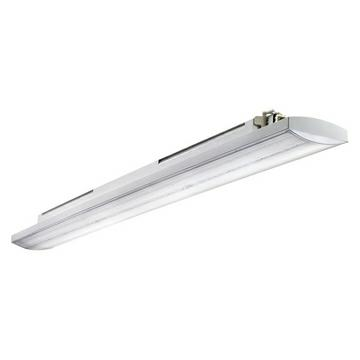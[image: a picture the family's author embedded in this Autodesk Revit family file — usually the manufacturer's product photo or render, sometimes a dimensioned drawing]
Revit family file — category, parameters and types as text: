
# Revit family: Lighting-Industrial-GEWISS-SMART[3]-WATERTIGHT-LED_TRASPARENT_1600mm
name_source: partatom
category: Apparecchi per illuminazione
units: mm (PartAtom-declared; Revit-internal decimal feet)

## family parameters
Condiviso = No
Host = Superficie
Punto di calcolo locali = Sì
Quota connettore circolare = Usa diametro
Sorgente d'illuminazione = No
Taglio con vuoti quando caricato = No
Tipo di parte = Normale

## types (1)
- Lighting-Industrial-GEWISS-SMART[3]-WATERTIGHT-LED_TRASPARENT_1600mm
    Application = Internal
    Catalogue = LIGHTING
    Catalogue Range = SMART [3]
    Colour temperature = 4000 K (CRI 80)
    Colour temperature: = 4000 K (CRI 80)
    Descrizione = SMART3 1600 72LED TRANSP DALI
    Device with reduced surface temperature = Complying
    Driver type = Constant Current Driver Led
    EAN code = 8011564869141
    Efficiency class of integrated LEDs = A ÷ A++
    Electrocod = 2434
    Failure rate apparecchio (35.000h, Tq=35° C) = <2,5%
    Failure rate apparecchio (50.000h, Tq=25° C) = <2,5%
    Ganci = GEWISS  - ALLUMINIO
    Glow Wire Test = 850°C
    IDF = 689142ee-b09e-4cde-8409-446d4916f831
    IDT = fad509ce-101b-4a7a-befe-b015b7d6ede8
    IP degree = IP66/IP69
    Immagine tipo = GWS3158T.jpg
    Insulation class = II
    LED Life Time (L90B50) = 50000H
    LED Life time (L70) = 80000H
    LED Life time (L80B50) = 100000H
    LED LifeTime (L80B20) = 85000H
    Lamp = LED
    Lampada = LED
    Length = 1600 mm
    Lumen output (lm) = 3400
    Lunghezza Lampada = 1600 mm  [stored 5.24934 ft]
    Modello = GWS3158TD
    No. LED (#) = 72
    Nominal flux (lm) = 3700
    Operating temperature: = -30 +50 °C
    Produttore = GEWISS S.p.A.
    Prospetto di default = 1219 mm
    SEO = Luminaire
    Schermo- = Gewiss - Led Acceso
    Shield type = Transparent
    Shock resistance = IK08
    Stampa 1_100 = Sì
    Stampa 1_200 = No
    Struttura = GEWISS - SMART 3 - GRIGIO
    System power = 26W
    Technical sheet = https://www.gewiss.com
    Type of light source = LED - Not replaceable
    Typology = DALI
    URL = https://www.gewiss.com
    Version file RFA = 20.11
    Voltage = 220/240 V - 50/60 Hz - Dali
    Warranty = 5 years
    Weight (kg): = 2,5
    Working temperature = -25 +50 °C

note: [stored X ft] marks values corroborated as IEEE doubles in the binary element streams (Revit-internal decimal feet)
